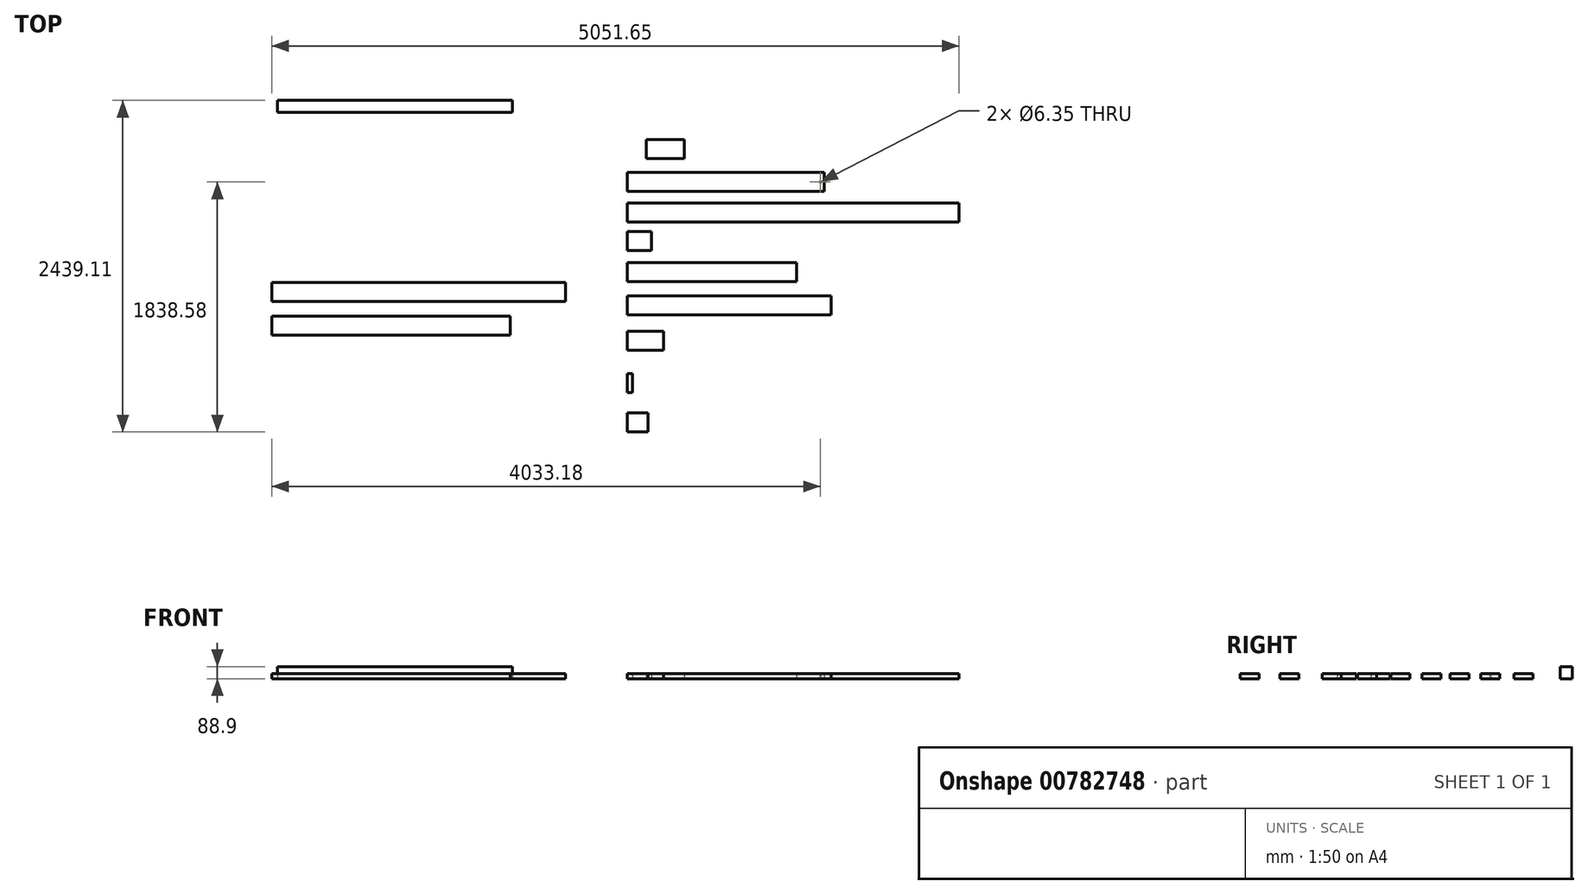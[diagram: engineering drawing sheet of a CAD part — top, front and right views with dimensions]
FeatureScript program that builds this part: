
annotation { "Feature Type Name" : "Feature", "Feature Type Description" : "" }
export const myFeature = defineFeature(function(context is Context, id is Id, definition is map)
    precondition{}
    {
        {
            var Q0;
            Q0=qCreatedBy(makeId("Top.planeOp"),FACE);
            var sketch = newSketch(context, id + "F0", { "sketchPlane" : qUnion([Q0])});
            skLineSegment(sketch, "E0.bottom", {"start": v(-293.96, 267.4) * mm, "end": v(-27.26, 267.4) * mm});
            skLineSegment(sketch, "E0.top", {"start": v(-293.96, 127.7) * mm, "end": v(-27.26, 127.7) * mm});
            skLineSegment(sketch, "E0.left", {"start": v(-293.96, 267.4) * mm, "end": v(-293.96, 127.7) * mm});
            skLineSegment(sketch, "E0.right", {"start": v(-27.26, 267.4) * mm, "end": v(-27.26, 127.7) * mm});
            skLineSegment(sketch, "E1.bottom", {"start": v(-293.96, -44.93) * mm, "end": v(-255.86, -44.93) * mm});
            skLineSegment(sketch, "E1.top", {"start": v(-293.96, -184.63) * mm, "end": v(-255.86, -184.63) * mm});
            skLineSegment(sketch, "E1.left", {"start": v(-293.96, -44.93) * mm, "end": v(-293.96, -184.63) * mm});
            skLineSegment(sketch, "E1.right", {"start": v(-255.86, -44.93) * mm, "end": v(-255.86, -184.63) * mm});
            skLineSegment(sketch, "E2.bottom", {"start": v(-293.96, -334.82) * mm, "end": v(-141.56, -334.82) * mm});
            skLineSegment(sketch, "E2.top", {"start": v(-293.96, -474.52) * mm, "end": v(-141.56, -474.52) * mm});
            skLineSegment(sketch, "E2.left", {"start": v(-293.96, -334.82) * mm, "end": v(-293.96, -474.52) * mm});
            skLineSegment(sketch, "E2.right", {"start": v(-141.56, -334.82) * mm, "end": v(-141.56, -474.52) * mm});
            skLineSegment(sketch, "E3.bottom", {"start": v(-293.96, 388.25) * mm, "end": v(1204.64, 388.25) * mm});
            skLineSegment(sketch, "E3.top", {"start": v(-293.96, 527.95) * mm, "end": v(1204.64, 527.95) * mm});
            skLineSegment(sketch, "E3.left", {"start": v(-293.96, 388.25) * mm, "end": v(-293.96, 527.95) * mm});
            skLineSegment(sketch, "E3.right", {"start": v(1204.64, 388.25) * mm, "end": v(1204.64, 527.95) * mm});
            skLineSegment(sketch, "E4.bottom", {"start": v(-293.96, 630.77) * mm, "end": v(950.64, 630.77) * mm});
            skLineSegment(sketch, "E4.top", {"start": v(-293.96, 770.47) * mm, "end": v(950.64, 770.47) * mm});
            skLineSegment(sketch, "E4.left", {"start": v(-293.96, 630.77) * mm, "end": v(-293.96, 770.47) * mm});
            skLineSegment(sketch, "E4.right", {"start": v(950.64, 630.77) * mm, "end": v(950.64, 770.47) * mm});
            skLineSegment(sketch, "E5.bottom", {"start": v(-293.96, 860.21) * mm, "end": v(-116.16, 860.21) * mm});
            skLineSegment(sketch, "E5.top", {"start": v(-293.96, 999.91) * mm, "end": v(-116.16, 999.91) * mm});
            skLineSegment(sketch, "E5.left", {"start": v(-293.96, 860.21) * mm, "end": v(-293.96, 999.91) * mm});
            skLineSegment(sketch, "E5.right", {"start": v(-116.16, 860.21) * mm, "end": v(-116.16, 999.91) * mm});
            skLineSegment(sketch, "E6.bottom", {"start": v(-293.96, 1068.68) * mm, "end": v(2144.44, 1068.68) * mm});
            skLineSegment(sketch, "E6.top", {"start": v(-293.96, 1208.38) * mm, "end": v(2144.44, 1208.38) * mm});
            skLineSegment(sketch, "E6.left", {"start": v(-293.96, 1068.68) * mm, "end": v(-293.96, 1208.38) * mm});
            skLineSegment(sketch, "E6.right", {"start": v(2144.44, 1068.68) * mm, "end": v(2144.44, 1208.38) * mm});
            skLineSegment(sketch, "E7.bottom", {"start": v(-293.96, 1294.21) * mm, "end": v(1153.84, 1294.21) * mm});
            skLineSegment(sketch, "E7.top", {"start": v(-293.96, 1433.91) * mm, "end": v(1153.84, 1433.91) * mm});
            skLineSegment(sketch, "E7.left", {"start": v(-293.96, 1294.21) * mm, "end": v(-293.96, 1433.91) * mm});
            skLineSegment(sketch, "E7.right", {"start": v(1153.84, 1294.21) * mm, "end": v(1153.84, 1433.91) * mm});
            skLineSegment(sketch, "E8.bottom", {"start": v(-293.96, 1536.7) * mm, "end": v(-14.56, 1536.7) * mm});
            skLineSegment(sketch, "E8.top", {"start": v(-293.96, 1676.4) * mm, "end": v(-14.56, 1676.4) * mm});
            skLineSegment(sketch, "E8.left", {"start": v(-293.96, 1536.7) * mm, "end": v(-293.96, 1676.4) * mm});
            skLineSegment(sketch, "E8.right", {"start": v(-14.56, 1536.7) * mm, "end": v(-14.56, 1676.4) * mm});
            skCircle(sketch, "E9", {"center": v(1125.97, 1364.06) * mm, "radius": 3.18 * mm});
            skPoint(sketch, "E9.centerSnap0", {"position": v(1153.84, 1364.06) * mm});
            skSolve(sketch);
        }
        {
            var Q0;
            Q0 = qSketchRegion(id + "F0", true);
            extrude(context, id + "F1", {"entities" : qUnion([Q0]), "depth" : 38.1 * mm, "offsetDistance" : 25.4 * mm});
        }
        {
            var Q0;
            Q0=makeQuery(id+"F1.opExtrude","SWEPT_FACE",FACE,{"disambiguationData":[OSD([sQuery(id+"F0.wireOp",EDGE,"E8.left")])]});
            extrude(context, id + "F2", {"entities" : qUnion([Q0]), "operationType" : NewBodyOperationType.REMOVE, "oppositeDirection" : true, "depth" : 139.7 * mm, "offsetDistance" : 25.4 * mm});
        }
        {
            var Q0;
            Q0=makeQuery(id+"F1.opExtrude","SWEPT_FACE",FACE,{"disambiguationData":[OSD([sQuery(id+"F0.wireOp",EDGE,"E8.right")])]});
            extrude(context, id + "F3", {"entities" : qUnion([Q0]), "operationType" : NewBodyOperationType.ADD, "depth" : 139.7 * mm, "offsetDistance" : 25.4 * mm});
        }
        {
            var Q0;
            Q0=qCreatedBy(makeId("Top.planeOp"),FACE);
            var sketch = newSketch(context, id + "F4", { "sketchPlane" : qUnion([Q0])});
            skLineSegment(sketch, "E10.bottom", {"start": v(-2907.21, 626.73) * mm, "end": v(-748.21, 626.73) * mm});
            skLineSegment(sketch, "E10.top", {"start": v(-2907.21, 487.03) * mm, "end": v(-748.21, 487.03) * mm});
            skLineSegment(sketch, "E10.left", {"start": v(-2907.21, 626.73) * mm, "end": v(-2907.21, 487.03) * mm});
            skLineSegment(sketch, "E10.right", {"start": v(-748.21, 626.73) * mm, "end": v(-748.21, 487.03) * mm});
            skLineSegment(sketch, "E11.bottom", {"start": v(-2907.21, 376.99) * mm, "end": v(-1154.61, 376.99) * mm});
            skLineSegment(sketch, "E11.top", {"start": v(-2907.21, 237.29) * mm, "end": v(-1154.61, 237.29) * mm});
            skLineSegment(sketch, "E11.left", {"start": v(-2907.21, 376.99) * mm, "end": v(-2907.21, 237.29) * mm});
            skLineSegment(sketch, "E11.right", {"start": v(-1154.61, 376.99) * mm, "end": v(-1154.61, 237.29) * mm});
            skSolve(sketch);
        }
        {
            var Q0;
            Q0 = qSketchRegion(id + "F4", true);
            extrude(context, id + "F5", {"entities" : qUnion([Q0]), "depth" : 38.1 * mm, "offsetDistance" : 25.4 * mm});
        }
        {
            var Q0;
            Q0=qCreatedBy(makeId("Top.planeOp"),FACE);
            var sketch = newSketch(context, id + "F6", { "sketchPlane" : qUnion([Q0])});
            skLineSegment(sketch, "E12.bottom", {"start": v(-2865.42, 1964.59) * mm, "end": v(-1138.22, 1964.59) * mm});
            skLineSegment(sketch, "E12.top", {"start": v(-2865.42, 1875.69) * mm, "end": v(-1138.22, 1875.69) * mm});
            skLineSegment(sketch, "E12.left", {"start": v(-2865.42, 1964.59) * mm, "end": v(-2865.42, 1875.69) * mm});
            skLineSegment(sketch, "E12.right", {"start": v(-1138.22, 1964.59) * mm, "end": v(-1138.22, 1875.69) * mm});
            skSolve(sketch);
        }
        {
            var Q0;
            Q0 = qSketchRegion(id + "F6", true);
            extrude(context, id + "F7", {"entities" : qUnion([Q0]), "depth" : 88.9 * mm, "offsetDistance" : 25.4 * mm});
        }
        {
            var Q0;
            Q0=makeQuery(id+"F1.opExtrude","SWEPT_BODY",BODY,{"disambiguationData":[OSD([sQuery(id+"F0.wireOp",EDGE,"E7.bottom"),sQuery(id+"F0.wireOp",EDGE,"E7.top"),sQuery(id+"F0.wireOp",EDGE,"E7.left"),sQuery(id+"F0.wireOp",EDGE,"E7.right"),sQuery(id+"F0.wireOp",EDGE,"E9")])]});
            transform(context, id + "F8", {"entities" : qUnion([Q0]), "transformType" : TransformType.TRANSLATION_3D, "dx" : 0 * mm, "dy" : 0 * mm, "dz" : 0 * mm, "makeCopy" : true});
        }
    });
